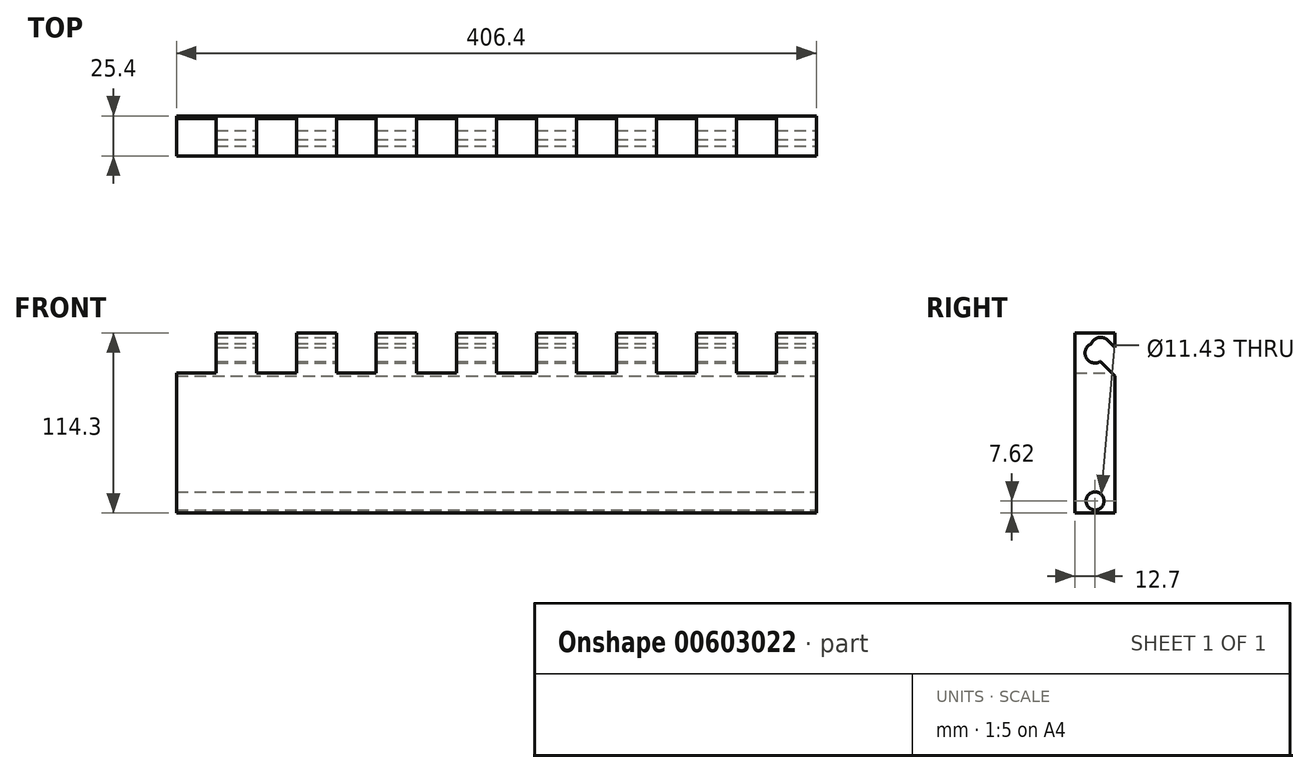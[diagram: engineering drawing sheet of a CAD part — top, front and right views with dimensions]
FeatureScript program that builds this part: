
annotation { "Feature Type Name" : "Feature", "Feature Type Description" : "" }
export const myFeature = defineFeature(function(context is Context, id is Id, definition is map)
    precondition{}
    {
        {
            var Q0;
            Q0=qCreatedBy(makeId("Front.planeOp"),FACE);
            var sketch = newSketch(context, id + "F0", { "sketchPlane" : qUnion([Q0])});
            skLineSegment(sketch, "E0.bottom", {"start": v(203.2, -57.15) * mm, "end": v(-203.2, -57.15) * mm});
            skLineSegment(sketch, "E0.top", {"start": v(203.2, 57.15) * mm, "end": v(-203.2, 57.15) * mm});
            skLineSegment(sketch, "E0.left", {"start": v(203.2, -57.15) * mm, "end": v(203.2, 57.15) * mm});
            skLineSegment(sketch, "E0.right", {"start": v(-203.2, -57.15) * mm, "end": v(-203.2, 57.15) * mm});
            skPoint(sketch, "E0.middle", {"position": v(0, 0) * mm});
            skLineSegment(sketch, "E1", {"start": v(-203.2, 57.15) * mm, "end": v(-203.2, 31.75) * mm});
            skLineSegment(sketch, "E2", {"start": v(-203.2, 31.75) * mm, "end": v(203.2, 31.75) * mm});
            skLineSegment(sketch, "E3", {"start": v(-203.2, 31.75) * mm, "end": v(-177.8, 31.75) * mm});
            skLineSegment(sketch, "E4", {"start": v(-177.8, 31.75) * mm, "end": v(-152.4, 31.75) * mm});
            skLineSegment(sketch, "E5", {"start": v(-152.4, 31.75) * mm, "end": v(-127, 31.75) * mm});
            skLineSegment(sketch, "E6", {"start": v(-127, 31.75) * mm, "end": v(-101.6, 31.75) * mm});
            skLineSegment(sketch, "E7", {"start": v(-101.6, 31.75) * mm, "end": v(-76.2, 31.75) * mm});
            skLineSegment(sketch, "E8", {"start": v(-76.2, 31.75) * mm, "end": v(-50.8, 31.75) * mm});
            skLineSegment(sketch, "E9", {"start": v(-50.8, 31.75) * mm, "end": v(-25.4, 31.75) * mm});
            skLineSegment(sketch, "E10", {"start": v(-25.4, 31.75) * mm, "end": v(0, 31.75) * mm});
            skLineSegment(sketch, "E11", {"start": v(0, 31.75) * mm, "end": v(25.4, 31.75) * mm});
            skLineSegment(sketch, "E12", {"start": v(25.4, 31.75) * mm, "end": v(50.8, 31.75) * mm});
            skLineSegment(sketch, "E13", {"start": v(50.8, 31.75) * mm, "end": v(76.2, 31.75) * mm});
            skLineSegment(sketch, "E14", {"start": v(76.2, 31.75) * mm, "end": v(101.6, 31.75) * mm});
            skLineSegment(sketch, "E15", {"start": v(101.6, 31.75) * mm, "end": v(127, 31.75) * mm});
            skLineSegment(sketch, "E16", {"start": v(127, 31.75) * mm, "end": v(152.4, 31.75) * mm});
            skLineSegment(sketch, "E17", {"start": v(152.4, 31.75) * mm, "end": v(177.8, 31.75) * mm});
            skLineSegment(sketch, "E18", {"start": v(177.8, 31.75) * mm, "end": v(203.2, 31.75) * mm});
            skLineSegment(sketch, "E19", {"start": v(-177.8, 31.75) * mm, "end": v(-177.8, 57.15) * mm});
            skLineSegment(sketch, "E20", {"start": v(-152.4, 31.75) * mm, "end": v(-152.4, 57.15) * mm});
            skLineSegment(sketch, "E21", {"start": v(-127, 31.75) * mm, "end": v(-127, 57.15) * mm});
            skLineSegment(sketch, "E22", {"start": v(-101.6, 31.75) * mm, "end": v(-101.6, 57.15) * mm});
            skLineSegment(sketch, "E23", {"start": v(-76.2, 31.75) * mm, "end": v(-76.2, 57.15) * mm});
            skLineSegment(sketch, "E24", {"start": v(-50.8, 31.75) * mm, "end": v(-50.8, 57.15) * mm});
            skLineSegment(sketch, "E25", {"start": v(-25.4, 31.75) * mm, "end": v(-25.4, 57.15) * mm});
            skLineSegment(sketch, "E26", {"start": v(0, 31.75) * mm, "end": v(0, 57.15) * mm});
            skLineSegment(sketch, "E27", {"start": v(25.4, 31.75) * mm, "end": v(25.4, 57.15) * mm});
            skLineSegment(sketch, "E28", {"start": v(50.8, 31.75) * mm, "end": v(50.8, 57.15) * mm});
            skLineSegment(sketch, "E29", {"start": v(76.2, 31.75) * mm, "end": v(76.2, 57.15) * mm});
            skLineSegment(sketch, "E30", {"start": v(101.6, 31.75) * mm, "end": v(101.6, 57.15) * mm});
            skLineSegment(sketch, "E31", {"start": v(127, 31.75) * mm, "end": v(127, 57.15) * mm});
            skLineSegment(sketch, "E32", {"start": v(152.4, 31.75) * mm, "end": v(152.4, 57.15) * mm});
            skLineSegment(sketch, "E33", {"start": v(177.8, 31.75) * mm, "end": v(177.8, 57.15) * mm});
            skSolve(sketch);
        }
        {
            var Q0;
            {var subQ10=sQuery(id+"F0.wireOp",EDGE,"E0.bottom");Q0=makeQuery(id+"F0.imprint","IMPRINT",FACE,{"disambiguationData":[TD([[makeQuery(id+"F0.imprint","IMPRINT",EDGE,{"derivedFrom":subQ10}),-1.0]])]});}
            var Q1;
            {var subQ3=sQuery(id+"F0.wireOp",EDGE,"E33");Q1=makeQuery(id+"F0.imprint","IMPRINT",FACE,{"disambiguationData":[TD([[makeQuery(id+"F0.imprint","IMPRINT",EDGE,{"derivedFrom":subQ3}),-1.0]])]});}
            var Q2;
            {var subQ0=sQuery(id+"F0.wireOp",EDGE,"E31");Q2=makeQuery(id+"F0.imprint","IMPRINT",FACE,{"disambiguationData":[TD([[makeQuery(id+"F0.imprint","IMPRINT",EDGE,{"derivedFrom":subQ0}),-1.0]])]});}
            var Q3;
            {var subQ0=sQuery(id+"F0.wireOp",EDGE,"E29");Q3=makeQuery(id+"F0.imprint","IMPRINT",FACE,{"disambiguationData":[TD([[makeQuery(id+"F0.imprint","IMPRINT",EDGE,{"derivedFrom":subQ0}),-1.0]])]});}
            var Q4;
            {var subQ0=sQuery(id+"F0.wireOp",EDGE,"E27");Q4=makeQuery(id+"F0.imprint","IMPRINT",FACE,{"disambiguationData":[TD([[makeQuery(id+"F0.imprint","IMPRINT",EDGE,{"derivedFrom":subQ0}),-1.0]])]});}
            var Q5;
            {var subQ0=sQuery(id+"F0.wireOp",EDGE,"E25");Q5=makeQuery(id+"F0.imprint","IMPRINT",FACE,{"disambiguationData":[TD([[makeQuery(id+"F0.imprint","IMPRINT",EDGE,{"derivedFrom":subQ0}),-1.0]])]});}
            var Q6;
            {var subQ0=sQuery(id+"F0.wireOp",EDGE,"E23");Q6=makeQuery(id+"F0.imprint","IMPRINT",FACE,{"disambiguationData":[TD([[makeQuery(id+"F0.imprint","IMPRINT",EDGE,{"derivedFrom":subQ0}),-1.0]])]});}
            var Q7;
            {var subQ2=sQuery(id+"F0.wireOp",EDGE,"E21");Q7=makeQuery(id+"F0.imprint","IMPRINT",FACE,{"disambiguationData":[TD([[makeQuery(id+"F0.imprint","IMPRINT",EDGE,{"derivedFrom":subQ2}),-1.0]])]});}
            var Q8;
            {var subQ0=sQuery(id+"F0.wireOp",EDGE,"E19");Q8=makeQuery(id+"F0.imprint","IMPRINT",FACE,{"disambiguationData":[TD([[makeQuery(id+"F0.imprint","IMPRINT",EDGE,{"derivedFrom":subQ0}),-1.0]])]});}
            extrude(context, id + "F1", {"entities" : qUnion([Q0, Q1, Q2, Q3, Q4, Q5, Q6, Q7, Q8]), "depth" : 25.4 * mm, "offsetDistance" : 25.4 * mm});
        }
        {
            var Q0;
            Q0=makeQuery(id+"F1.opExtrude","SWEPT_FACE",FACE,{"disambiguationData":[OSD([sQuery(id+"F0.wireOp",EDGE,"E0.left")])]});
            var sketch = newSketch(context, id + "F2", { "sketchPlane" : qUnion([Q0])});
            skLineSegment(sketch, "E34", {"start": v(-12.7, 57.15) * mm, "end": v(-12.7, 44.45) * mm});
            skCircle(sketch, "E35", {"center": v(-12.7, 44.45) * mm, "radius": 6.35 * mm});
            skLineSegment(sketch, "E36", {"start": v(-12.7, 44.45) * mm, "end": v(-17.2, 39.96) * mm});
            skLineSegment(sketch, "E37", {"start": v(-12.7, 44.45) * mm, "end": v(-8.2, 48.94) * mm});
            skLineSegment(sketch, "E38", {"start": v(-17.2, 39.96) * mm, "end": v(0, 22.77) * mm});
            skLineSegment(sketch, "E39", {"start": v(-8.2, 48.94) * mm, "end": v(0, 40.73) * mm});
            skLineSegment(sketch, "E40", {"start": v(-17.2, 39.96) * mm, "end": v(-13.6, 43.55) * mm});
            skLineSegment(sketch, "E41", {"start": v(-13.6, 43.55) * mm, "end": v(0, 29.95) * mm});
            skLineSegment(sketch, "E42", {"start": v(-8.2, 48.94) * mm, "end": v(-4.62, 52.53) * mm});
            skLineSegment(sketch, "E43", {"start": v(-4.62, 52.53) * mm, "end": v(0, 47.91) * mm});
            skArc(sketch, "E44", {"start": v(-4.62, 52.53) * mm, "mid": v(-13.6, 52.53) * mm, "end": v(-13.6, 43.55) * mm});
            skSolve(sketch);
        }
        {
            var Q0;
            Q0 = qSketchRegion(id + "F2", true);
            var Q1;
            {var subQ0=sQuery(id+"F2.wireOp",EDGE,"E39");var subQ1=sQuery(id+"F2.wireOp",EDGE,"E35");var subQ2=makeQuery(id+"F2.imprint","INTERSECT",VERTEX,{"derivedFrom":[subQ1,subQ0]});Q1=makeQuery(id+"F2.imprint","IMPRINT",FACE,{"disambiguationData":[TD([[makeQuery(id+"F2.imprint","IMPRINT",EDGE,{"disambiguationData":[TD([[subQ2,1.0]])],"derivedFrom":subQ1}),-1.0]])]});}
            var Q2;
            {var subQ0=sQuery(id+"F2.wireOp",EDGE,"E39");Q2=makeQuery(id+"F2.imprint","IMPRINT",FACE,{"disambiguationData":[TD([[makeQuery(id+"F2.imprint","IMPRINT",EDGE,{"derivedFrom":subQ0}),1.0]])]});}
            extrude(context, id + "F3", {"entities" : qUnion([Q0, Q1, Q2]), "operationType" : NewBodyOperationType.REMOVE, "oppositeDirection" : true, "depth" : 412.75 * mm, "offsetDistance" : 25.4 * mm});
        }
        {
            var Q0;
            Q0=makeQuery(id+"F1.opExtrude","SWEPT_FACE",FACE,{"disambiguationData":[OSD([sQuery(id+"F0.wireOp",EDGE,"E0.left")])]});
            var sketch = newSketch(context, id + "F4", { "sketchPlane" : qUnion([Q0])});
            skLineSegment(sketch, "E45", {"start": v(-12.7, -57.15) * mm, "end": v(-12.7, -49.53) * mm});
            skCircle(sketch, "E46", {"center": v(-12.7, -49.53) * mm, "radius": 5.72 * mm});
            skSolve(sketch);
        }
        {
            var Q0;
            Q0 = qSketchRegion(id + "F4", true);
            extrude(context, id + "F5", {"entities" : qUnion([Q0]), "operationType" : NewBodyOperationType.REMOVE, "oppositeDirection" : true, "depth" : 598.93 * mm, "offsetDistance" : 25.4 * mm});
        }
    });
